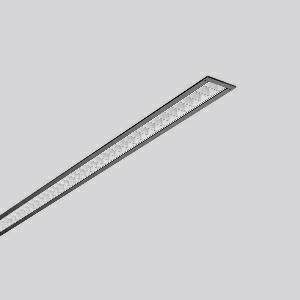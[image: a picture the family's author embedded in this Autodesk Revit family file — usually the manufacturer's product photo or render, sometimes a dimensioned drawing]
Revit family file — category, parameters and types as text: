
# Revit family: less_is_more_27_312179_003_1_76_1901
name_source: partatom
category: Lighting Fixtures
units: mm (PartAtom-declared; Revit-internal decimal feet)

## family parameters
Cut with Voids When Loaded = No
Host = Face
Light Source = No
Part Type = Normal
Room Calculation Point = No
Round Connector Dimension = Use Diameter
Shared = No

## types (1)
- LESS IS MORE 27 (1 x LED Modul 840, 3500 lm, 4000)
    Apparent Load = 39 VA
    CIE Flux Codes = 90 99 100 100 100
    Color Rendering = 80
    Color Temperature = 4000
    Default Elevation = 1800 mm
    Description = Series: LESS IS MORE 27
Recessed ceiling and wall luminaire with slim design. Housing: extruded aluminium profile, powder-coated. End cap aluminium powder-coated. High polish aluminium micro grid. Perfect for office areas (RUG < 19) and environments with computer screens in accordance with EN 12464-1. Suitable for Recessed ceiling mounting, wall (recessed). External driver with connecting cable. 
Colour: deep black, matt (RAL 9005)
Length: 1514 mm
Width: 38 mm
Height: 2 mm
Cut-out length: 1506 mm
Cut-out width: 30 mm
Recess height: 45-60 mm
Luminaire: recess height: 37 mm
Lamp: LED
Socket: without socket
Colour temperature: 4000K
Colour rendering index (CRI): 82
System power: 39 W
Rated luminous flux: 3500 lm
Luminous efficiency: 90 lm/W
Control gear: Voltage converter, DALI dim.
Protection class: II
Type of protection: IP 20
    Height = 0 mm  [stored 0 ft]
    Lamp = 1 x LED Modul 840
    Lamp Light Flux = 3500 lm
    Lamp count = 1
    Length = 1514 mm
    Lifetime = 50000 h
    Luminous efficacy = 90 lm/W
    Manufacturer = RZB
    ModVariant = No
    Model = 312179.003.1.76
    Mounting Place = Ceiling, Wall
    Mounting Type = Recessed
    Number of Poles = 1
    OnlyDefault = Yes
    Power Factor = 1
    Product Name = LESS IS MORE 27
    Product group = Recessed LED linear luminaires
    ProductGroupID = 407
    Protection Class = Protection class II
    Protection Degree = IP 20
    RLX_Detail_Level = 1
    RLX_Emergency_Light_Flux = 0 lm
    RLX_Emergency_Type = 0
    RLX_Emergency_Type_DB = No
    RlxData = <blob elided: 29917 chars, md5=1c50501a>
    Socket = socket
    Standby Power = 0 W
    System Light Flux = 3500 lm
    System Power = 39 W
    Type Comments = Product without accessories
    Type Image = 312177.003.jpg
    URL = http://relux.com
    VarID = ---
    Voltage = 230 V
    Voltage Range = 220-240 V
    Weight = 0.00 kg
    Width = 38 mm

note: [stored X ft] marks values corroborated as IEEE doubles in the binary element streams (Revit-internal decimal feet)

## geometry (parser evidence)
native form markers: Blend x4, Sweep x11
no freeform markers — native parametric forms only
